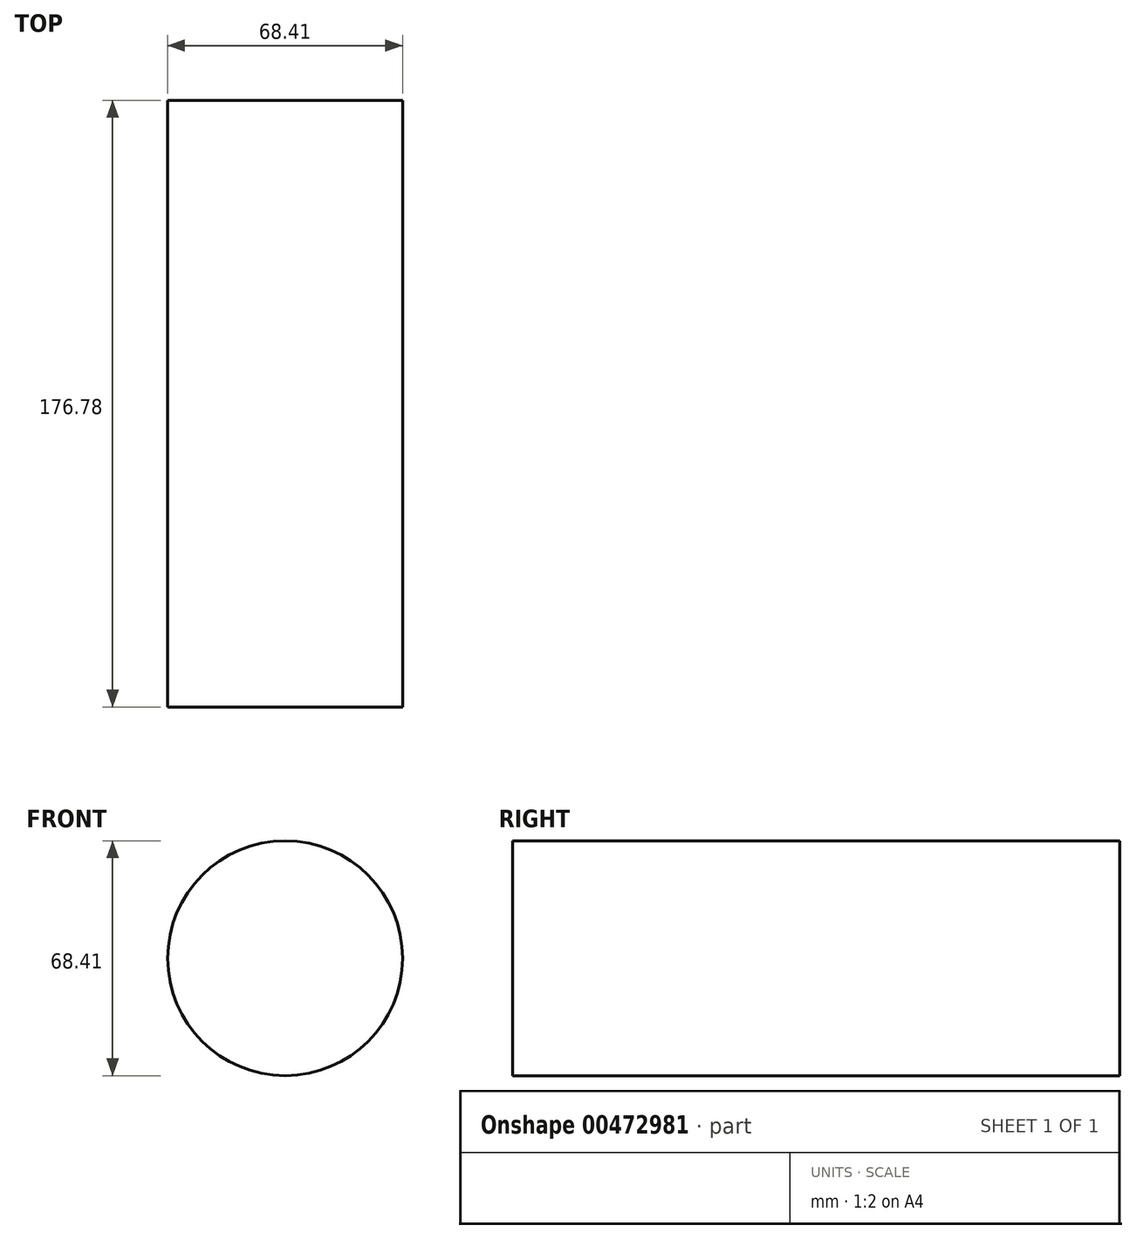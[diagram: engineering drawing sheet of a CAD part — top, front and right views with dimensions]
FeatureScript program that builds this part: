
annotation { "Feature Type Name" : "Feature", "Feature Type Description" : "" }
export const myFeature = defineFeature(function(context is Context, id is Id, definition is map)
    precondition{}
    {
        {
            var Q0;
            Q0=qCreatedBy(makeId("Front.planeOp"),FACE);
            var sketch = newSketch(context, id + "F0", { "sketchPlane" : qUnion([Q0])});
            skCircle(sketch, "E0", {"center": v(-51.45, 47.44) * mm, "radius": 34.2 * mm});
            skSolve(sketch);
        }
        {
            var Q0;
            Q0 = qSketchRegion(id + "F0", true);
            var Q1;
            Q1=makeQuery(id+"F0.imprint","IMPRINT",FACE,{"disambiguationData":[TD([[makeQuery(id+"F0.imprint","IMPRINT",EDGE,{"derivedFrom":sQuery(id+"F0.wireOp",EDGE,"E0")}),1.0]])]});
            extrude(context, id + "F1", {"entities" : qUnion([Q0, Q1]), "depth" : 176.78 * mm});
        }
    });
